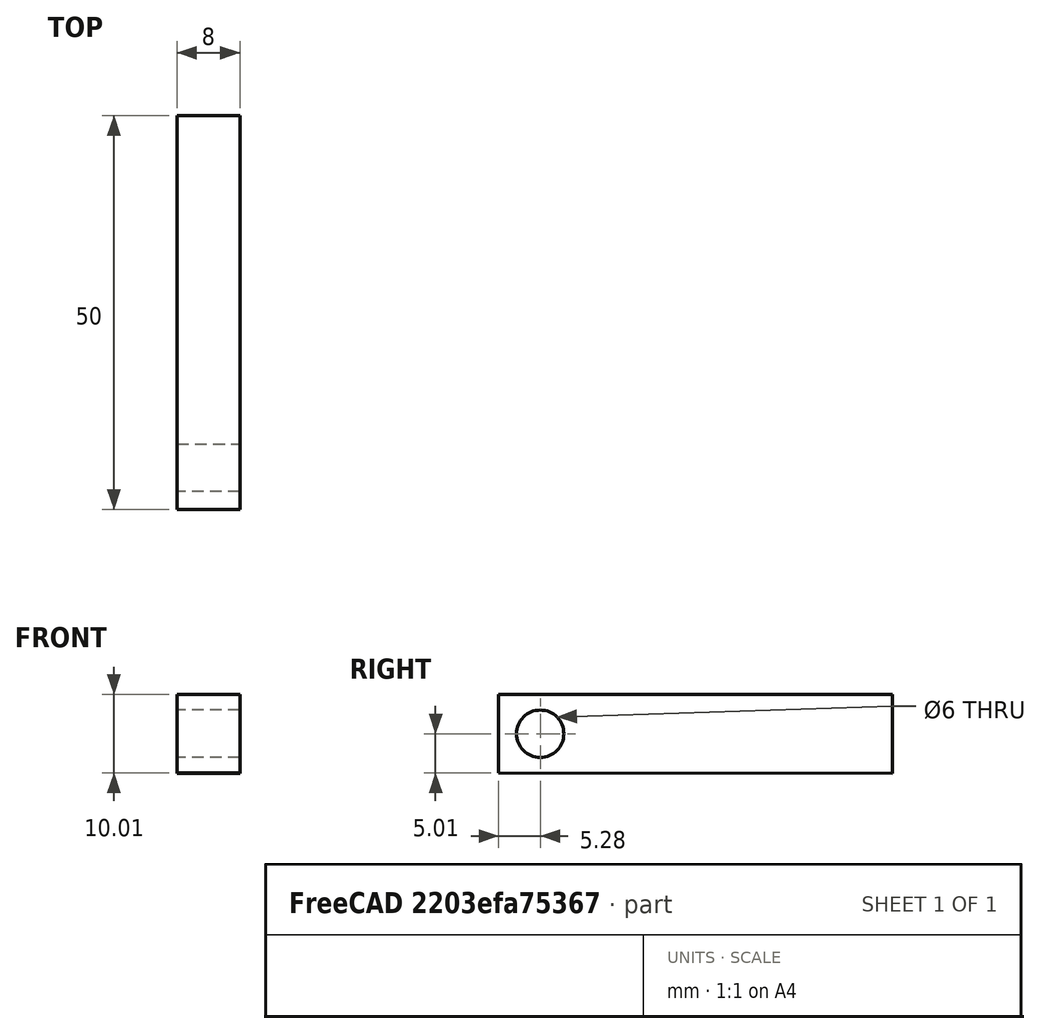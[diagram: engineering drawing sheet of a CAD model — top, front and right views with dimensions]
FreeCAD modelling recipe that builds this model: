
FCSTD DOCUMENT  (FreeCAD 0.21R33668 +26 (Git))
Label: Assembly_000
License: All rights reserved
LicenseURL: http://en.wikipedia.org/wiki/All_rights_reserved
objects: PartDesign::CoordinateSystem×4, App::DocumentObjectGroup×3, Sketcher::SketchObject×2, App::Link×2, App::FeaturePython×1, PartDesign::Pad×1, PartDesign::Body×1, App::Part×1
note: 9 computed .brp shape members not serialized (recipe doc carries the construction recipe); baked Part::Feature solids carry a one-line shape summary decoded from their .brp

FEATURE [PartDesign::CoordinateSystem] LCS_Origin
  AttacherType = Attacher::AttachEngine3D
  MapMode = 2
  Support = -> [X_Axis]
FEATURE [App::DocumentObjectGroup] Constraints
FEATURE [App::FeaturePython] Variables  # WARN: FeaturePython — macro-defined, semantics opaque (R4)
  Type = App::PropertyContainer
  rotation_bielle_1 = 45
  rotation_bielle_2 = 90
FEATURE [App::DocumentObjectGroup] Configurations
FEATURE [PartDesign::CoordinateSystem] LCS_0
  AttacherType = Attacher::AttachEngine3D
  MapMode = 2
  Support = -> [X_Axis001]
FEATURE [Sketcher::SketchObject] Sketch
  FullyConstrained = false
  MapMode = 5
  Placement = pos=(0,0,0) rot=(0.57735,0.57735,0.57735;2.0944rad)
  Support = -> [YZ_Plane001]
  sketch-geometry (5):
    g0: LineSegment StartX=-5.27726 StartY=5.00146 StartZ=0 EndX=44.7227 EndY=4.98767 EndZ=0
    g1: LineSegment StartX=44.7227 StartY=4.98767 StartZ=0 EndX=44.72 EndY=-5.01233 EndZ=0
    g2: LineSegment StartX=44.72 StartY=-5.01233 StartZ=0 EndX=-5.28002 EndY=-4.99854 EndZ=0
    g3: LineSegment StartX=-5.28002 StartY=-4.99854 StartZ=0 EndX=-5.27726 EndY=5.00146 EndZ=0
    g4: Circle CenterX=0 CenterY=0 CenterZ=0 NormalX=0 NormalY=0 NormalZ=1 AngleXU=0 Radius=3
  constraints (13):
    c: Coincident(g0,g1)
    c: Coincident(g1,g2)
    c: Coincident(g2,g3)
    c: Coincident(g3,g0)
    c: Distance(g0,g2) = 10
    c: Distance(g0,g0) = 50
    c: Parallel(g0,g2)
    c: Parallel(g3,g1)
    c: Perpendicular(g0,g1)
    c: Coincident(g4,g-1)
    c: Radius(g4) = 3
    c: Distance(g4,g0) = 45
    c: Distance(g4,g1) = 45
FEATURE [PartDesign::Pad] Pad
  Direction = (1,-2e-16,3e-16)
  Length = 8
  Length2 = 10
  Placement = pos=(0,0,0) rot=(1,1,1;2.0944rad)
  Profile = -> Sketch
  ReferenceAxis = -> Sketch [N_Axis]
  Type = 0
FEATURE [PartDesign::Body] Body
  Group = -> [LCS_0,Sketch,Pad]
  Origin = -> Origin001
  Placement = pos=(-52,0,0) rot=(0,0,1;0rad)
  Tip = -> Pad
FEATURE [App::DocumentObjectGroup] Parts
  Group = -> [Body]
FEATURE [Sketcher::SketchObject] Sketch_1
  FullyConstrained = true
  MapMode = 5
  Placement = pos=(0,0,0) rot=(0.57735,0.57735,0.57735;2.0944rad)
  Support = -> [YZ_Plane]
  expr: Constraints[1] = Variables.rotation_bielle_1
  expr: Constraints[5] = Variables.rotation_bielle_2
  sketch-geometry (2):
    g0: LineSegment StartX=0 StartY=0 StartZ=0 EndX=24.7487 EndY=24.7487 EndZ=0
    g1: LineSegment StartX=0 StartY=0 StartZ=0 EndX=-2.68009e-10 EndY=-50 EndZ=0
  constraints (6):
    c: Coincident(g0,g-1)
    c: Angle(g-1,g0) = 0.785398
    c: Distance(g0,g0) = 35
    c: Coincident(g1,g0)
    c: Distance(g0,g1) = 50
    c: Angle(g1,g-1) = 1.5708
FEATURE [PartDesign::CoordinateSystem] LCS_1  label="LCS_bielle_1"
  AttacherType = Attacher::AttachEngine3D
  MapMode = 7
  Support = -> [Sketch_1]
FEATURE [App::Link] Body001
  AttachedBy = #LCS_0
  AttachedTo = Parent Assembly#LCS_1
  AttachmentOffset = pos=(0,0,0) rot=(1,0,0;4.71239rad)
  LinkPlacement = pos=(0,0,0) rot=(1,0,0;4.71239rad)
  LinkedObject = -> Body
  Placement = pos=(0,0,0) rot=(1,0,0;4.71239rad)
  SolverId = Asm4EE
  expr: Placement = LCS_1.Placement * AttachmentOffset * LCS_0.Placement ^ -1
FEATURE [PartDesign::CoordinateSystem] LCS_bielle_2
  AttacherType = Attacher::AttachEngine3D
  MapMode = 7
  Placement = pos=(0,0,0) rot=(1,0,0;2.35619rad)
  Support = -> [Sketch_1]
FEATURE [App::Link] Body002
  AttachedBy = #LCS_0
  AttachedTo = Parent Assembly#LCS_bielle_2
  AttachmentOffset = pos=(0,0,0) rot=(1,0,0;4.71239rad)
  LinkPlacement = pos=(0,0,0) rot=(-1,0,0;5.49779rad)
  LinkedObject = -> Body
  Placement = pos=(0,0,0) rot=(-1,0,0;5.49779rad)
  SolverId = Asm4EE
  expr: Placement = LCS_bielle_2.Placement * AttachmentOffset * LCS_0.Placement ^ -1
FEATURE [App::Part] Assembly
  AssemblyType = Part::Link
  Group = -> [LCS_Origin,Constraints,Variables,Configurations,Sketch_1,LCS_1,Body001,LCS_bielle_2,Body002]
  Origin = -> Origin
  Type = Assembly
